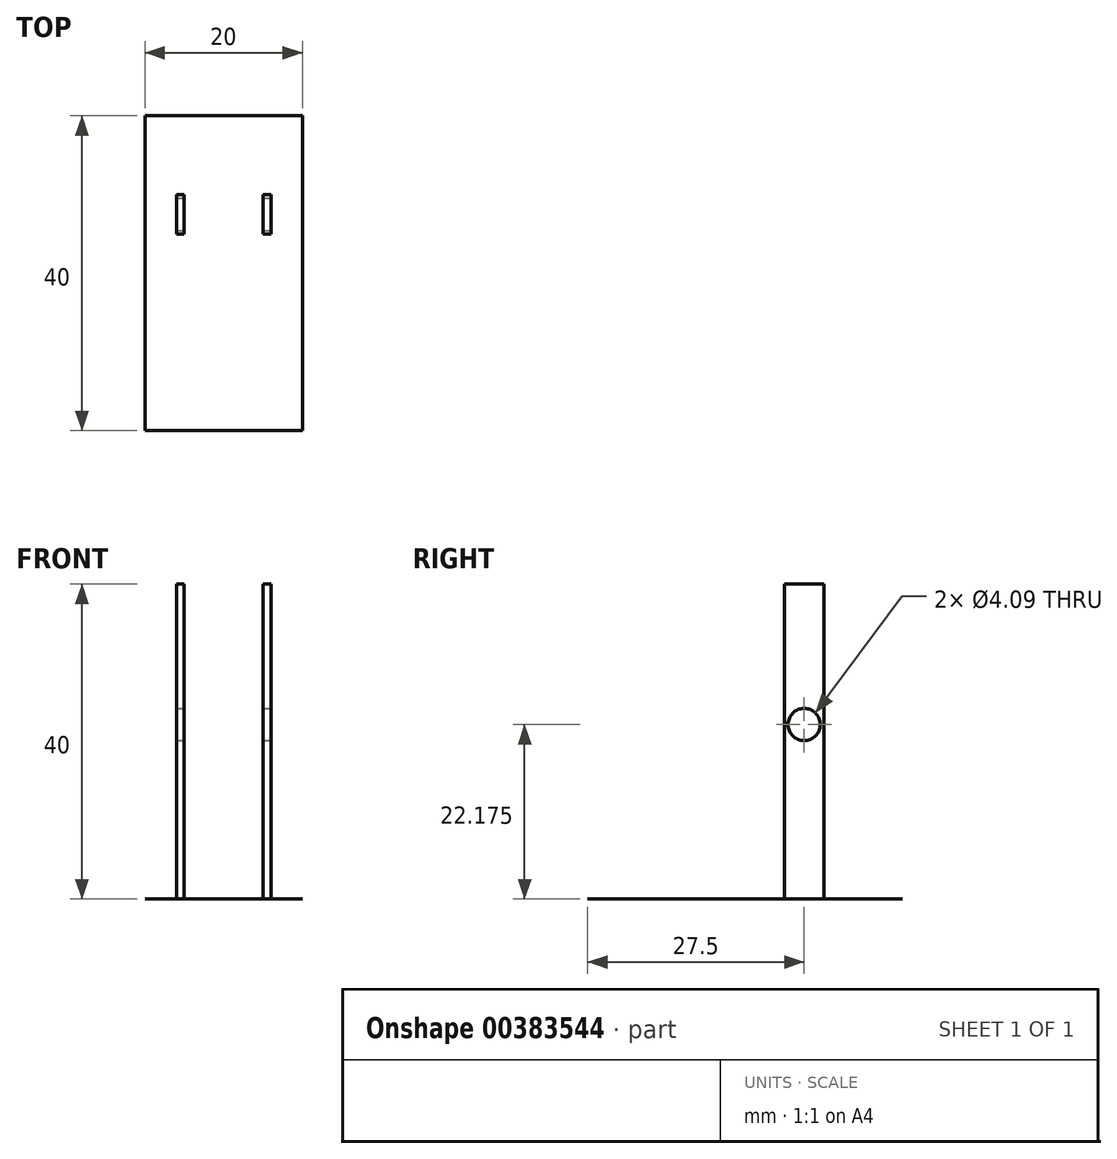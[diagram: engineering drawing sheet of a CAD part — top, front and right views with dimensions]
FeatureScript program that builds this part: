
annotation { "Feature Type Name" : "Feature", "Feature Type Description" : "" }
export const myFeature = defineFeature(function(context is Context, id is Id, definition is map)
    precondition{}
    {
        {
            var Q0;
            Q0=qCreatedBy(makeId("Top.planeOp"),FACE);
            var sketch = newSketch(context, id + "F0", { "sketchPlane" : qUnion([Q0])});
            skLineSegment(sketch, "E0.bottom", {"start": v(10, 20) * mm, "end": v(-10, 20) * mm});
            skLineSegment(sketch, "E0.top", {"start": v(10, -20) * mm, "end": v(-10, -20) * mm});
            skLineSegment(sketch, "E0.left", {"start": v(10, 20) * mm, "end": v(10, -20) * mm});
            skLineSegment(sketch, "E0.right", {"start": v(-10, 20) * mm, "end": v(-10, -20) * mm});
            skPoint(sketch, "E0.middle", {"position": v(0, 0) * mm});
            skLineSegment(sketch, "E1", {"start": v(-6, 10) * mm, "end": v(-5, 10) * mm});
            skLineSegment(sketch, "E2", {"start": v(-6, 5) * mm, "end": v(-5, 5) * mm});
            skLineSegment(sketch, "E3", {"start": v(-5, 10) * mm, "end": v(-5, 5) * mm});
            skLineSegment(sketch, "E4", {"start": v(-6, 10) * mm, "end": v(-6, 5) * mm});
            skLineSegment(sketch, "E5.MirrorCS", {"start": v(5, 10) * mm, "end": v(5, 5) * mm});
            skLineSegment(sketch, "E6.MirrorCS", {"start": v(6, 10) * mm, "end": v(6, 5) * mm});
            skPoint(sketch, "E7.orphan", {"position": v(-5, 20) * mm});
            skPoint(sketch, "E8.orphan", {"position": v(-6, 20) * mm});
            skPoint(sketch, "E9.orphan", {"position": v(-6, -20) * mm});
            skPoint(sketch, "E10.orphan", {"position": v(-5, -20) * mm});
            skPoint(sketch, "E11.orphan", {"position": v(5, -20) * mm});
            skPoint(sketch, "E12.orphan", {"position": v(6, -20) * mm});
            skPoint(sketch, "E13.orphan", {"position": v(6, 20) * mm});
            skPoint(sketch, "E14.orphan", {"position": v(5, 20) * mm});
            skLineSegment(sketch, "E15.trimOffspring", {"start": v(5, 5) * mm, "end": v(6, 5) * mm});
            skPoint(sketch, "E16.orphan", {"position": v(-10, 10) * mm});
            skLineSegment(sketch, "E17.trimOffspring", {"start": v(5, 10) * mm, "end": v(6, 10) * mm});
            skPoint(sketch, "E18.orphan", {"position": v(10, 5) * mm});
            skSolve(sketch);
        }
        {
            var Q0;
            Q0=makeQuery(id+"F0.imprint","IMPRINT",FACE,{"disambiguationData":[TD([[makeQuery(id+"F0.imprint","IMPRINT",EDGE,{"derivedFrom":sQuery(id+"F0.wireOp",EDGE,"E0.bottom")}),1.0]])]});
            extrude(context, id + "F1", {"entities" : qUnion([Q0]), "depth" : 1 / 203.2 * mm});
        }
        {
            var Q0;
            Q0=makeQuery(id+"F0.imprint","IMPRINT",FACE,{"disambiguationData":[TD([[makeQuery(id+"F0.imprint","IMPRINT",EDGE,{"derivedFrom":sQuery(id+"F0.wireOp",EDGE,"E1")}),-1.0]])]});
            var Q1;
            Q1=makeQuery(id+"F0.imprint","IMPRINT",FACE,{"disambiguationData":[TD([[makeQuery(id+"F0.imprint","IMPRINT",EDGE,{"derivedFrom":sQuery(id+"F0.wireOp",EDGE,"E5.MirrorCS")}),1.0]])]});
            extrude(context, id + "F2", {"entities" : qUnion([Q0, Q1]), "operationType" : NewBodyOperationType.ADD, "depth" : 40 * mm});
        }
        {
            var Q0;
            Q0=makeQuery(id+"F2.opExtrude","SWEPT_FACE",FACE,{"disambiguationData":[OSD([sQuery(id+"F0.wireOp",EDGE,"E6.MirrorCS")])]});
            var sketch = newSketch(context, id + "F3", { "sketchPlane" : qUnion([Q0])});
            skCircle(sketch, "E19", {"center": v(7.5, 22.18) * mm, "radius": 1.57 * mm});
            skLineSegment(sketch, "E20", {"start": v(7.5, 40) * mm, "end": v(7.5, 3.18) * mm});
            skSolve(sketch);
        }
        {
            var Q0;
            Q0=sQuery(id+"F3.wireOp",VERTEX,"E19.center");
            var Q1;
            Q1=makeQuery(id+"F1.opExtrude","SWEPT_BODY",BODY,{"disambiguationData":[OSD([sQuery(id+"F0.wireOp",EDGE,"E0.bottom"),sQuery(id+"F0.wireOp",EDGE,"E0.top"),sQuery(id+"F0.wireOp",EDGE,"E0.left"),sQuery(id+"F0.wireOp",EDGE,"E0.right"),sQuery(id+"F0.wireOp",EDGE,"E1"),sQuery(id+"F0.wireOp",EDGE,"E2"),sQuery(id+"F0.wireOp",EDGE,"E3"),sQuery(id+"F0.wireOp",EDGE,"E4"),sQuery(id+"F0.wireOp",EDGE,"E5.MirrorCS"),sQuery(id+"F0.wireOp",EDGE,"E6.MirrorCS"),sQuery(id+"F0.wireOp",EDGE,"E15.trimOffspring"),sQuery(id+"F0.wireOp",EDGE,"E17.trimOffspring")])]});
            hole(context, id + "F4", {"style" : HoleStyle.SIMPLE, "endStyle" : HoleEndStyle.THROUGH, "standardTappedOrClearance" : lookupTablePath({ "standard" : "ANSI", "size" : "#20 (0.16)", "type" : "Drilled" }), "standardBlindInLast" : lookupTablePath({ "standard" : "ANSI", "size" : "#20", "type" : "Drilled" }), "holeDiameter" : 4.1 * mm, "isTappedThrough" : true, "tappedDepth" : 12.7 * mm, "tapClearance" : 3, "locations" : qUnion([Q0]), "scope" : qUnion([Q1])});
        }
    });
